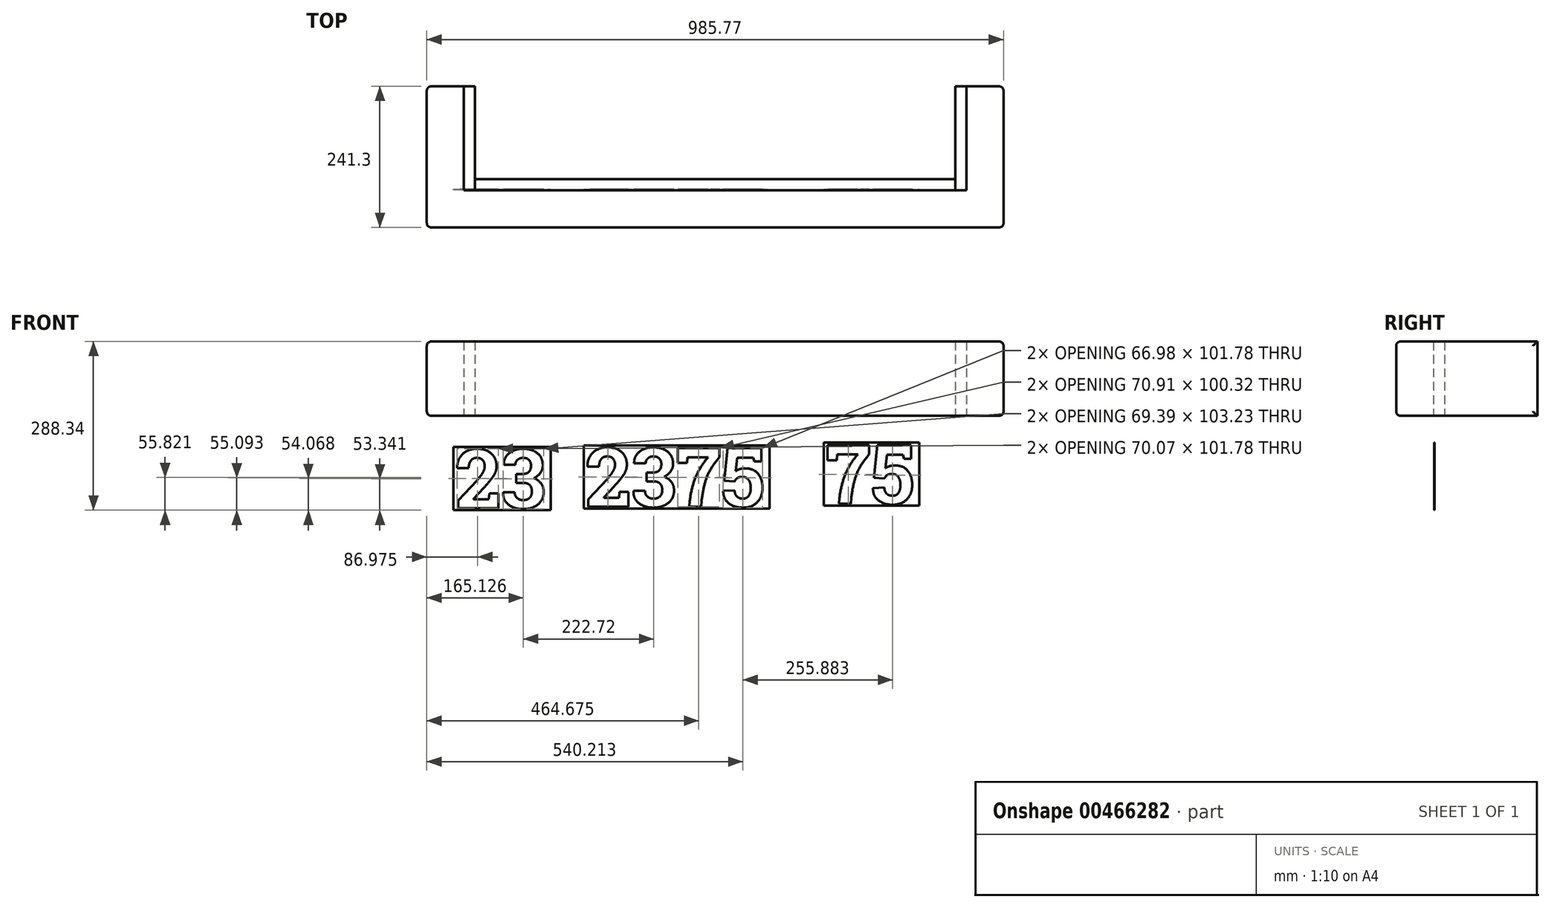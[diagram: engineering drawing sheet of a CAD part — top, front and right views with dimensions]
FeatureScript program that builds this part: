
annotation { "Feature Type Name" : "Feature", "Feature Type Description" : "" }
export const myFeature = defineFeature(function(context is Context, id is Id, definition is map)
    precondition{}
    {
        {
            var Q0;
            Q0=qCreatedBy(makeId("Top.planeOp"),FACE);
            var sketch = newSketch(context, id + "F0", { "sketchPlane" : qUnion([Q0])});
            skLineSegment(sketch, "E0.bottom", {"start": v(-363.57, 16.88) * mm, "end": v(457.1, 16.88) * mm});
            skLineSegment(sketch, "E0.top", {"start": v(-363.57, -65.67) * mm, "end": v(355.5, -65.67) * mm});
            skLineSegment(sketch, "E1", {"start": v(-363.57, 16.88) * mm, "end": v(-363.57, 175.63) * mm});
            skLineSegment(sketch, "E2", {"start": v(-363.57, 175.63) * mm, "end": v(-446.12, 175.63) * mm});
            skLineSegment(sketch, "E3", {"start": v(-446.12, 175.63) * mm, "end": v(-446.12, -65.67) * mm});
            skLineSegment(sketch, "E4", {"start": v(-446.12, -65.67) * mm, "end": v(-363.57, -65.67) * mm});
            skLineSegment(sketch, "E5", {"start": v(457.1, 16.88) * mm, "end": v(457.1, 175.63) * mm});
            skLineSegment(sketch, "E6", {"start": v(457.1, 175.63) * mm, "end": v(539.65, 175.63) * mm});
            skLineSegment(sketch, "E7", {"start": v(539.65, 175.63) * mm, "end": v(539.65, -65.67) * mm});
            skLineSegment(sketch, "E8", {"start": v(539.65, -65.67) * mm, "end": v(355.5, -65.67) * mm});
            skLineSegment(sketch, "E9", {"start": v(-363.57, -2.17) * mm, "end": v(457.1, -2.17) * mm});
            skLineSegment(sketch, "E10", {"start": v(-363.57, -2.17) * mm, "end": v(-382.62, -2.17) * mm});
            skLineSegment(sketch, "E11", {"start": v(-382.62, -2.17) * mm, "end": v(-382.62, 175.63) * mm});
            skLineSegment(sketch, "E12", {"start": v(457.1, -2.17) * mm, "end": v(476.15, -2.17) * mm});
            skLineSegment(sketch, "E13", {"start": v(476.15, -2.17) * mm, "end": v(476.15, 175.63) * mm});
            skLineSegment(sketch, "E14", {"start": v(-382.62, -2.17) * mm, "end": v(-382.62, -65.67) * mm});
            skLineSegment(sketch, "E15", {"start": v(476.15, -2.17) * mm, "end": v(476.15, -65.67) * mm});
            skLineSegment(sketch, "E16", {"start": v(-363.57, -2.17) * mm, "end": v(-363.57, 16.88) * mm});
            skLineSegment(sketch, "E17", {"start": v(457.1, 16.88) * mm, "end": v(457.1, -2.17) * mm});
            skSolve(sketch);
        }
        {
            var Q0;
            {var subQ1=sQuery(id+"F0.wireOp",EDGE,"E3");Q0=makeQuery(id+"F0.imprint","IMPRINT",FACE,{"disambiguationData":[TD([[makeQuery(id+"F0.imprint","IMPRINT",EDGE,{"derivedFrom":subQ1}),1.0]])]});}
            var Q1;
            {var subQ1=sQuery(id+"F0.wireOp",EDGE,"E0.top");Q1=makeQuery(id+"F0.imprint","IMPRINT",FACE,{"disambiguationData":[TD([[makeQuery(id+"F0.imprint","IMPRINT",EDGE,{"derivedFrom":subQ1}),1.0]])]});}
            var Q2;
            {var subQ2=sQuery(id+"F0.wireOp",EDGE,"E7");Q2=makeQuery(id+"F0.imprint","IMPRINT",FACE,{"disambiguationData":[TD([[makeQuery(id+"F0.imprint","IMPRINT",EDGE,{"derivedFrom":subQ2}),-1.0]])]});}
            extrude(context, id + "F1", {"entities" : qUnion([Q0, Q1, Q2]), "depth" : 127 * mm});
        }
        {
            var Q0;
            Q0=makeQuery(id+"F1.opExtrude","CAP_EDGE",EDGE,{"disambiguationData":[OSD([sQuery(id+"F0.wireOp",EDGE,"E3")])],"isStart":false});
            var Q1;
            Q1=makeQuery(id+"F1.opExtrude","CAP_EDGE",EDGE,{"disambiguationData":[OSD([sQuery(id+"F0.wireOp",EDGE,"E0.top"),sQuery(id+"F0.wireOp",EDGE,"E4"),sQuery(id+"F0.wireOp",EDGE,"E8")])],"isStart":false});
            var Q2;
            Q2=makeQuery(id+"F1.opExtrude","CAP_EDGE",EDGE,{"disambiguationData":[OSD([sQuery(id+"F0.wireOp",EDGE,"E7")])],"isStart":false});
            var Q3;
            Q3=makeQuery(id+"F1.opExtrude","SWEPT_EDGE",EDGE,{"disambiguationData":[OSD([sQuery(id+"F0.wireOp",EDGE,"E6"),sQuery(id+"F0.wireOp",EDGE,"E7")])]});
            var Q4;
            Q4=makeQuery(id+"F1.opExtrude","CAP_EDGE",EDGE,{"disambiguationData":[OSD([sQuery(id+"F0.wireOp",EDGE,"E7")])],"isStart":true});
            var Q5;
            Q5=makeQuery(id+"F1.opExtrude","CAP_EDGE",EDGE,{"disambiguationData":[OSD([sQuery(id+"F0.wireOp",EDGE,"E0.top"),sQuery(id+"F0.wireOp",EDGE,"E4"),sQuery(id+"F0.wireOp",EDGE,"E8")])],"isStart":true});
            var Q6;
            Q6=makeQuery(id+"F1.opExtrude","CAP_EDGE",EDGE,{"disambiguationData":[OSD([sQuery(id+"F0.wireOp",EDGE,"E3")])],"isStart":true});
            var Q7;
            Q7=makeQuery(id+"F1.opExtrude","SWEPT_EDGE",EDGE,{"disambiguationData":[OSD([sQuery(id+"F0.wireOp",EDGE,"E2"),sQuery(id+"F0.wireOp",EDGE,"E3")])]});
            var Q8;
            Q8=makeQuery(id+"F1.opExtrude","SWEPT_EDGE",EDGE,{"disambiguationData":[OSD([sQuery(id+"F0.wireOp",EDGE,"E3"),sQuery(id+"F0.wireOp",EDGE,"E4")])]});
            var Q9;
            Q9=makeQuery(id+"F1.opExtrude","SWEPT_EDGE",EDGE,{"disambiguationData":[OSD([sQuery(id+"F0.wireOp",EDGE,"E7"),sQuery(id+"F0.wireOp",EDGE,"E8")])]});
            fillet(context, id + "F2", {"entities" : qUnion([Q0, Q1, Q2, Q3, Q4, Q5, Q6, Q7, Q8, Q9]), "radius" : 7.62 * mm, "tangentPropagation" : true, "allowEdgeOverflow" : false});
        }
        {
            var Q0;
            {var subQ2=sQuery(id+"F0.wireOp",EDGE,"E1");Q0=makeQuery(id+"F0.imprint","IMPRINT",FACE,{"disambiguationData":[TD([[makeQuery(id+"F0.imprint","IMPRINT",EDGE,{"derivedFrom":subQ2}),1.0]])]});}
            extrude(context, id + "F3", {"entities" : qUnion([Q0]), "depth" : 127 * mm});
        }
        {
            var Q0;
            Q0=makeQuery(id+"F0.imprint","IMPRINT",FACE,{"disambiguationData":[TD([[makeQuery(id+"F0.imprint","IMPRINT",EDGE,{"derivedFrom":sQuery(id+"F0.wireOp",EDGE,"E0.bottom")}),-1.0]])]});
            extrude(context, id + "F4", {"entities" : qUnion([Q0]), "depth" : 127 * mm});
        }
        {
            var Q0;
            {var subQ1=sQuery(id+"F0.wireOp",EDGE,"E5");Q0=makeQuery(id+"F0.imprint","IMPRINT",FACE,{"disambiguationData":[TD([[makeQuery(id+"F0.imprint","IMPRINT",EDGE,{"derivedFrom":subQ1}),-1.0]])]});}
            extrude(context, id + "F5", {"entities" : qUnion([Q0]), "depth" : 127 * mm});
        }
        {
            var Q0;
            Q0=qCreatedBy(makeId("Front.planeOp"),FACE);
            var sketch = newSketch(context, id + "F6", { "sketchPlane" : qUnion([Q0])});
            skText(sketch, "E18", { "text": "2375", "fontName": "RobotoSlab-Bold.ttf"});
            skLineSegment(sketch, "E19.bottom", {"start": v(-178.07, -50.9) * mm, "end": v(139.4, -50.9) * mm});
            skLineSegment(sketch, "E19.top", {"start": v(-178.07, -158.86) * mm, "end": v(139.4, -158.86) * mm});
            skLineSegment(sketch, "E19.left", {"start": v(-178.07, -50.9) * mm, "end": v(-178.07, -158.86) * mm});
            skLineSegment(sketch, "E19.right", {"start": v(139.4, -50.9) * mm, "end": v(139.4, -158.86) * mm});
            skText(sketch, "E20", { "text": "75", "fontName": "RobotoSlab-Bold.ttf"});
            skText(sketch, "E21", { "text": "23", "fontName": "RobotoSlab-Bold.ttf"});
            skLineSegment(sketch, "E22.bottom", {"start": v(-400.8, -53.39) * mm, "end": v(-234.48, -53.39) * mm});
            skLineSegment(sketch, "E22.top", {"start": v(-400.8, -161.34) * mm, "end": v(-234.48, -161.34) * mm});
            skLineSegment(sketch, "E22.left", {"start": v(-400.8, -53.39) * mm, "end": v(-400.8, -161.34) * mm});
            skLineSegment(sketch, "E22.right", {"start": v(-234.48, -53.39) * mm, "end": v(-234.48, -161.34) * mm});
            skLineSegment(sketch, "E23.bottom", {"start": v(232.44, -45.94) * mm, "end": v(395.29, -45.94) * mm});
            skLineSegment(sketch, "E23.top", {"start": v(232.44, -153.9) * mm, "end": v(395.29, -153.9) * mm});
            skLineSegment(sketch, "E23.left", {"start": v(232.44, -45.94) * mm, "end": v(232.44, -153.9) * mm});
            skLineSegment(sketch, "E23.right", {"start": v(395.29, -45.94) * mm, "end": v(395.29, -153.9) * mm});
            const initialGuessF6  = {"E18": [-0.1749, -0.15568, 1, 0, 0.1016], "E20": [0.23561, -0.15072, 1, 0, 0.1016], "E21": [-0.39762, -0.15816, 1, 0, 0.1016]};
            skSetInitialGuess(sketch, initialGuessF6);
            skSolve(sketch);
        }
        {
            var Q0;
            Q0=makeQuery(id+"F6.imprint","IMPRINT",FACE,{"disambiguationData":[TD([[makeQuery(id+"F6.imprint","IMPRINT",EDGE,{"derivedFrom":sQuery(id+"F6.wireOp",EDGE,"E18.sketch_text.stroke-0")}),-1.0]])]});
            var Q1;
            Q1=makeQuery(id+"F6.imprint","IMPRINT",FACE,{"disambiguationData":[TD([[makeQuery(id+"F6.imprint","IMPRINT",EDGE,{"derivedFrom":sQuery(id+"F6.wireOp",EDGE,"E18.sketch_text.stroke-23")}),-1.0]])]});
            var Q2;
            Q2=makeQuery(id+"F6.imprint","IMPRINT",FACE,{"disambiguationData":[TD([[makeQuery(id+"F6.imprint","IMPRINT",EDGE,{"derivedFrom":sQuery(id+"F6.wireOp",EDGE,"E18.sketch_text.stroke-54")}),-1.0]])]});
            var Q3;
            Q3=makeQuery(id+"F6.imprint","IMPRINT",FACE,{"disambiguationData":[TD([[makeQuery(id+"F6.imprint","IMPRINT",EDGE,{"derivedFrom":sQuery(id+"F6.wireOp",EDGE,"E18.sketch_text.stroke-67")}),-1.0]])]});
            var Q4;
            Q4=makeQuery(id+"F6.imprint","IMPRINT",FACE,{"disambiguationData":[TD([[makeQuery(id+"F6.imprint","IMPRINT",EDGE,{"derivedFrom":sQuery(id+"F6.wireOp",EDGE,"E21.sketch_text.stroke-0")}),-1.0]])]});
            var Q5;
            Q5=makeQuery(id+"F6.imprint","IMPRINT",FACE,{"disambiguationData":[TD([[makeQuery(id+"F6.imprint","IMPRINT",EDGE,{"derivedFrom":sQuery(id+"F6.wireOp",EDGE,"E21.sketch_text.stroke-23")}),-1.0]])]});
            var Q6;
            Q6=makeQuery(id+"F6.imprint","IMPRINT",FACE,{"disambiguationData":[TD([[makeQuery(id+"F6.imprint","IMPRINT",EDGE,{"derivedFrom":sQuery(id+"F6.wireOp",EDGE,"E20.sketch_text.stroke-0")}),-1.0]])]});
            var Q7;
            Q7=makeQuery(id+"F6.imprint","IMPRINT",FACE,{"disambiguationData":[TD([[makeQuery(id+"F6.imprint","IMPRINT",EDGE,{"derivedFrom":sQuery(id+"F6.wireOp",EDGE,"E20.sketch_text.stroke-13")}),-1.0]])]});
            extrude(context, id + "F7", {"entities" : qUnion([Q0, Q1, Q2, Q3, Q4, Q5, Q6, Q7]), "depth" : 0.8 * mm});
        }
        {
            var Q0;
            Q0=makeQuery(id+"F6.imprint","IMPRINT",FACE,{"disambiguationData":[TD([[makeQuery(id+"F6.imprint","IMPRINT",EDGE,{"derivedFrom":sQuery(id+"F6.wireOp",EDGE,"E18.sketch_text.stroke-0")}),1.0]])]});
            var Q1;
            Q1=makeQuery(id+"F6.imprint","IMPRINT",FACE,{"disambiguationData":[TD([[makeQuery(id+"F6.imprint","IMPRINT",EDGE,{"derivedFrom":sQuery(id+"F6.wireOp",EDGE,"E21.sketch_text.stroke-0")}),1.0]])]});
            var Q2;
            Q2=makeQuery(id+"F6.imprint","IMPRINT",FACE,{"disambiguationData":[TD([[makeQuery(id+"F6.imprint","IMPRINT",EDGE,{"derivedFrom":sQuery(id+"F6.wireOp",EDGE,"E20.sketch_text.stroke-0")}),1.0]])]});
            extrude(context, id + "F8", {"entities" : qUnion([Q0, Q1, Q2]), "depth" : 0.8 * mm});
        }
    });
